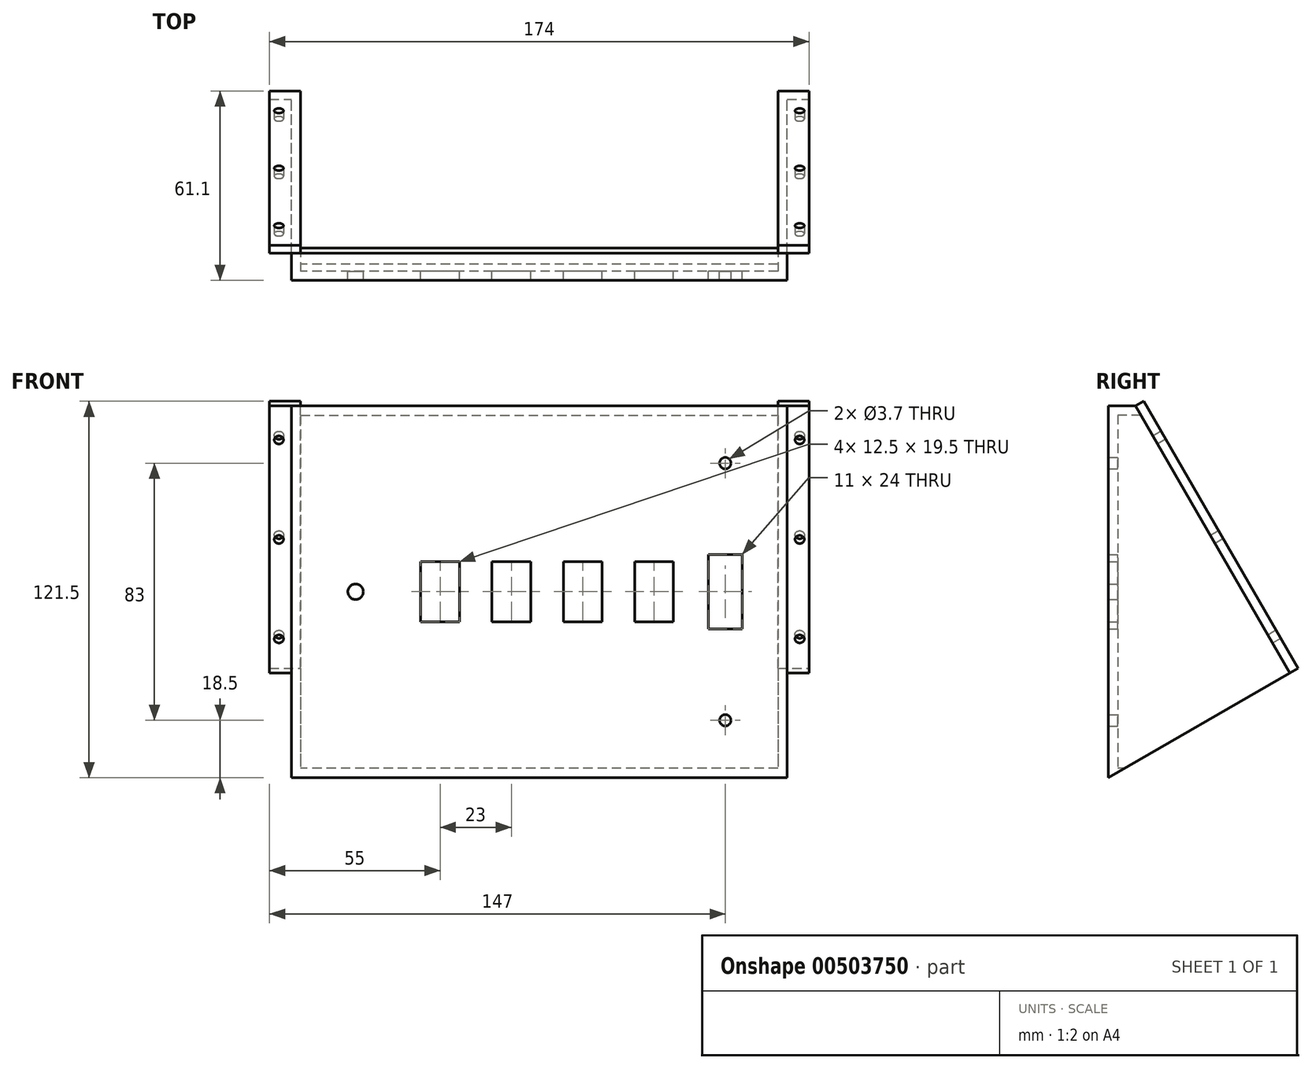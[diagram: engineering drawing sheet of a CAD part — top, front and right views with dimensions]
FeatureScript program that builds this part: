
annotation { "Feature Type Name" : "Feature", "Feature Type Description" : "" }
export const myFeature = defineFeature(function(context is Context, id is Id, definition is map)
    precondition{}
    {
        {
            var Q0;
            Q0=qCreatedBy(makeId("Front.planeOp"),FACE);
            var sketch = newSketch(context, id + "F0", { "sketchPlane" : qUnion([Q0])});
            skLineSegment(sketch, "E0.bottom", {"start": v(80, 60) * mm, "end": v(-80, 60) * mm});
            skLineSegment(sketch, "E0.top", {"start": v(80, -60) * mm, "end": v(-80, -60) * mm});
            skLineSegment(sketch, "E0.left", {"start": v(80, 60) * mm, "end": v(80, -60) * mm});
            skLineSegment(sketch, "E0.right", {"start": v(-80, 60) * mm, "end": v(-80, -60) * mm});
            skPoint(sketch, "E0.middle", {"position": v(0, 0) * mm});
            skLineSegment(sketch, "E1", {"start": v(-80, 0) * mm, "end": v(80, 0) * mm, "construction": true});
            skLineSegment(sketch, "E2.bottom", {"start": v(65.5, -12) * mm, "end": v(54.5, -12) * mm});
            skLineSegment(sketch, "E2.top", {"start": v(65.5, 12) * mm, "end": v(54.5, 12) * mm});
            skLineSegment(sketch, "E2.left", {"start": v(65.5, -12) * mm, "end": v(65.5, 12) * mm});
            skLineSegment(sketch, "E2.right", {"start": v(54.5, -12) * mm, "end": v(54.5, 12) * mm});
            skPoint(sketch, "E2.middle", {"position": v(60, 0) * mm});
            skCircle(sketch, "E3", {"center": v(60, 41.5) * mm, "radius": 1.85 * mm});
            skCircle(sketch, "E4", {"center": v(60, -41.5) * mm, "radius": 1.85 * mm});
            skPoint(sketch, "E4.centerSnap0", {"position": v(60, -12) * mm});
            skLineSegment(sketch, "E5.bottom", {"start": v(43.25, 9.75) * mm, "end": v(30.75, 9.75) * mm});
            skLineSegment(sketch, "E5.top", {"start": v(43.25, -9.75) * mm, "end": v(30.75, -9.75) * mm});
            skLineSegment(sketch, "E5.left", {"start": v(43.25, 9.75) * mm, "end": v(43.25, -9.75) * mm});
            skLineSegment(sketch, "E5.right", {"start": v(30.75, 9.75) * mm, "end": v(30.75, -9.75) * mm});
            skPoint(sketch, "E5.middle", {"position": v(37, 0) * mm});
            skLineSegment(sketch, "E6.1.0.0", {"start": v(20.25, 9.75) * mm, "end": v(7.75, 9.75) * mm});
            skLineSegment(sketch, "E6.1.0.1", {"start": v(7.75, 9.75) * mm, "end": v(7.75, -9.75) * mm});
            skLineSegment(sketch, "E6.1.0.2", {"start": v(20.25, -9.75) * mm, "end": v(7.75, -9.75) * mm});
            skLineSegment(sketch, "E6.1.0.3", {"start": v(20.25, 9.75) * mm, "end": v(20.25, -9.75) * mm});
            skLineSegment(sketch, "E6.2.0.0", {"start": v(-2.75, 9.75) * mm, "end": v(-15.25, 9.75) * mm});
            skLineSegment(sketch, "E6.2.0.1", {"start": v(-15.25, 9.75) * mm, "end": v(-15.25, -9.75) * mm});
            skLineSegment(sketch, "E6.2.0.2", {"start": v(-2.75, -9.75) * mm, "end": v(-15.25, -9.75) * mm});
            skLineSegment(sketch, "E6.2.0.3", {"start": v(-2.75, 9.75) * mm, "end": v(-2.75, -9.75) * mm});
            skLineSegment(sketch, "E6.3.0.0", {"start": v(-25.75, 9.75) * mm, "end": v(-38.25, 9.75) * mm});
            skLineSegment(sketch, "E6.3.0.1", {"start": v(-38.25, 9.75) * mm, "end": v(-38.25, -9.75) * mm});
            skLineSegment(sketch, "E6.3.0.2", {"start": v(-25.75, -9.75) * mm, "end": v(-38.25, -9.75) * mm});
            skLineSegment(sketch, "E6.3.0.3", {"start": v(-25.75, 9.75) * mm, "end": v(-25.75, -9.75) * mm});
            skLineSegment(sketch, "E6.direction1", {"start": v(30.75, 9.75) * mm, "end": v(7.75, 9.75) * mm, "construction": true});
            skCircle(sketch, "E7", {"center": v(-59.27, 0) * mm, "radius": 2.5 * mm});
            skSolve(sketch);
        }
        {
            var Q0;
            Q0 = qSketchRegion(id + "F0", true);
            extrude(context, id + "F1", {"entities" : qUnion([Q0]), "depth" : 3 * mm, "offsetDistance" : 25 * mm});
        }
        {
            var Q0;
            Q0=makeQuery(id+"F1.opExtrude","CAP_FACE",FACE,{"disambiguationData":[OSD([sQuery(id+"F0.wireOp",EDGE,"E0.bottom"),sQuery(id+"F0.wireOp",EDGE,"E0.top"),sQuery(id+"F0.wireOp",EDGE,"E0.left"),sQuery(id+"F0.wireOp",EDGE,"E0.right"),sQuery(id+"F0.wireOp",EDGE,"E2.bottom"),sQuery(id+"F0.wireOp",EDGE,"E2.top"),sQuery(id+"F0.wireOp",EDGE,"E2.left"),sQuery(id+"F0.wireOp",EDGE,"E2.right"),sQuery(id+"F0.wireOp",EDGE,"E3"),sQuery(id+"F0.wireOp",EDGE,"E4"),sQuery(id+"F0.wireOp",EDGE,"E5.bottom"),sQuery(id+"F0.wireOp",EDGE,"E5.top"),sQuery(id+"F0.wireOp",EDGE,"E5.left"),sQuery(id+"F0.wireOp",EDGE,"E5.right"),sQuery(id+"F0.wireOp",EDGE,"E6.1.0.0"),sQuery(id+"F0.wireOp",EDGE,"E6.1.0.1"),sQuery(id+"F0.wireOp",EDGE,"E6.1.0.2"),sQuery(id+"F0.wireOp",EDGE,"E6.1.0.3"),sQuery(id+"F0.wireOp",EDGE,"E6.2.0.0"),sQuery(id+"F0.wireOp",EDGE,"E6.2.0.1"),sQuery(id+"F0.wireOp",EDGE,"E6.2.0.2"),sQuery(id+"F0.wireOp",EDGE,"E6.2.0.3"),sQuery(id+"F0.wireOp",EDGE,"E6.3.0.0"),sQuery(id+"F0.wireOp",EDGE,"E6.3.0.1"),sQuery(id+"F0.wireOp",EDGE,"E6.3.0.2"),sQuery(id+"F0.wireOp",EDGE,"E6.3.0.3"),sQuery(id+"F0.wireOp",EDGE,"E6.4.0.0"),sQuery(id+"F0.wireOp",EDGE,"E6.4.0.1"),sQuery(id+"F0.wireOp",EDGE,"E6.4.0.2"),sQuery(id+"F0.wireOp",EDGE,"E6.4.0.3")])],"isStart":true});
            var sketch = newSketch(context, id + "F2", { "sketchPlane" : qUnion([Q0])});
            skLineSegment(sketch, "E8.bottom", {"start": v(-80, 60) * mm, "end": v(80, 60) * mm});
            skLineSegment(sketch, "E8.top", {"start": v(-80, -60) * mm, "end": v(80, -60) * mm});
            skLineSegment(sketch, "E8.left", {"start": v(-80, 60) * mm, "end": v(-80, -60) * mm});
            skLineSegment(sketch, "E8.right", {"start": v(80, 60) * mm, "end": v(80, -60) * mm});
            skLineSegment(sketch, "E9.0", {"start": v(-77, 57) * mm, "end": v(77, 57) * mm});
            skLineSegment(sketch, "E9.1", {"start": v(-77, 57) * mm, "end": v(-77, -57) * mm});
            skLineSegment(sketch, "E9.2", {"start": v(-77, -57) * mm, "end": v(77, -57) * mm});
            skLineSegment(sketch, "E9.3", {"start": v(77, 57) * mm, "end": v(77, -57) * mm});
            skSolve(sketch);
        }
        {
            var Q0;
            Q0 = qSketchRegion(id + "F2", true);
            extrude(context, id + "F3", {"entities" : qUnion([Q0]), "operationType" : NewBodyOperationType.ADD, "depth" : 75 * mm, "offsetDistance" : 25 * mm});
        }
        {
            var Q0;
            Q0=makeQuery(id+"F3.boolean.opBoolean","MERGE",FACE,{"derivedFrom":[makeQuery(id+"F1.opExtrude","SWEPT_FACE",FACE,{"disambiguationData":[OSD([sQuery(id+"F0.wireOp",EDGE,"E0.left")])]}),makeQuery(id+"F3.opExtrude","SWEPT_FACE",FACE,{"disambiguationData":[OSD([sQuery(id+"F2.wireOp",EDGE,"E8.left")])]})]});
            var sketch = newSketch(context, id + "F4", { "sketchPlane" : qUnion([Q0])});
            skLineSegment(sketch, "E10", {"start": v(5.72, 60) * mm, "end": v(55.5, -26.23) * mm});
            skLineSegment(sketch, "E11", {"start": v(75, -60) * mm, "end": v(75, 60) * mm});
            skLineSegment(sketch, "E12", {"start": v(75, 60) * mm, "end": v(5.72, 60) * mm});
            skLineSegment(sketch, "E13", {"start": v(-3, -60) * mm, "end": v(55.5, -26.23) * mm});
            skLineSegment(sketch, "E14", {"start": v(-3, -60) * mm, "end": v(75, -60) * mm});
            skSolve(sketch);
        }
        {
            var Q0;
            Q0 = qSketchRegion(id + "F4", true);
            extrude(context, id + "F5", {"entities" : qUnion([Q0]), "operationType" : NewBodyOperationType.REMOVE, "endBound" : BoundingType.THROUGH_ALL, "oppositeDirection" : true, "depth" : 25 * mm, "offsetDistance" : 25 * mm});
        }
        {
            var Q0;
            Q0=makeQuery(id+"F5.boolean.opBoolean","COPY",FACE,{"derivedFrom":makeQuery(id+"F5.opExtrude","SWEPT_FACE",FACE,{"disambiguationData":[OSD([sQuery(id+"F4.wireOp",EDGE,"E10")])]})});
            var sketch = newSketch(context, id + "F6", { "sketchPlane" : qUnion([Q0])});
            skLineSegment(sketch, "E15.bottom", {"start": v(-77, -50.46) * mm, "end": v(-87, -50.46) * mm});
            skLineSegment(sketch, "E15.top", {"start": v(-77, 49.1) * mm, "end": v(-87, 49.1) * mm});
            skLineSegment(sketch, "E15.left", {"start": v(-77, -50.46) * mm, "end": v(-77, 49.1) * mm});
            skLineSegment(sketch, "E15.right", {"start": v(-87, -50.46) * mm, "end": v(-87, 49.1) * mm});
            skLineSegment(sketch, "E16.bottom", {"start": v(77, -50.46) * mm, "end": v(87, -50.46) * mm});
            skLineSegment(sketch, "E16.top", {"start": v(77, 49.1) * mm, "end": v(87, 49.1) * mm});
            skLineSegment(sketch, "E16.left", {"start": v(77, -50.46) * mm, "end": v(77, 49.1) * mm});
            skLineSegment(sketch, "E16.right", {"start": v(87, -50.46) * mm, "end": v(87, 49.1) * mm});
            skCircle(sketch, "E17", {"center": v(-84, 36.4) * mm, "radius": 1.5 * mm});
            skCircle(sketch, "E18", {"center": v(-84, -0.68) * mm, "radius": 1.5 * mm});
            skCircle(sketch, "E19", {"center": v(-84, -37.76) * mm, "radius": 1.5 * mm});
            skCircle(sketch, "E20", {"center": v(84, 36.4) * mm, "radius": 1.5 * mm});
            skCircle(sketch, "E21", {"center": v(84, -0.68) * mm, "radius": 1.5 * mm});
            skCircle(sketch, "E22", {"center": v(84, -37.76) * mm, "radius": 1.5 * mm});
            skSolve(sketch);
        }
        {
            var Q0;
            Q0 = qSketchRegion(id + "F6", true);
            extrude(context, id + "F7", {"entities" : qUnion([Q0]), "operationType" : NewBodyOperationType.ADD, "depth" : 3 * mm, "offsetDistance" : 25 * mm});
        }
    });
